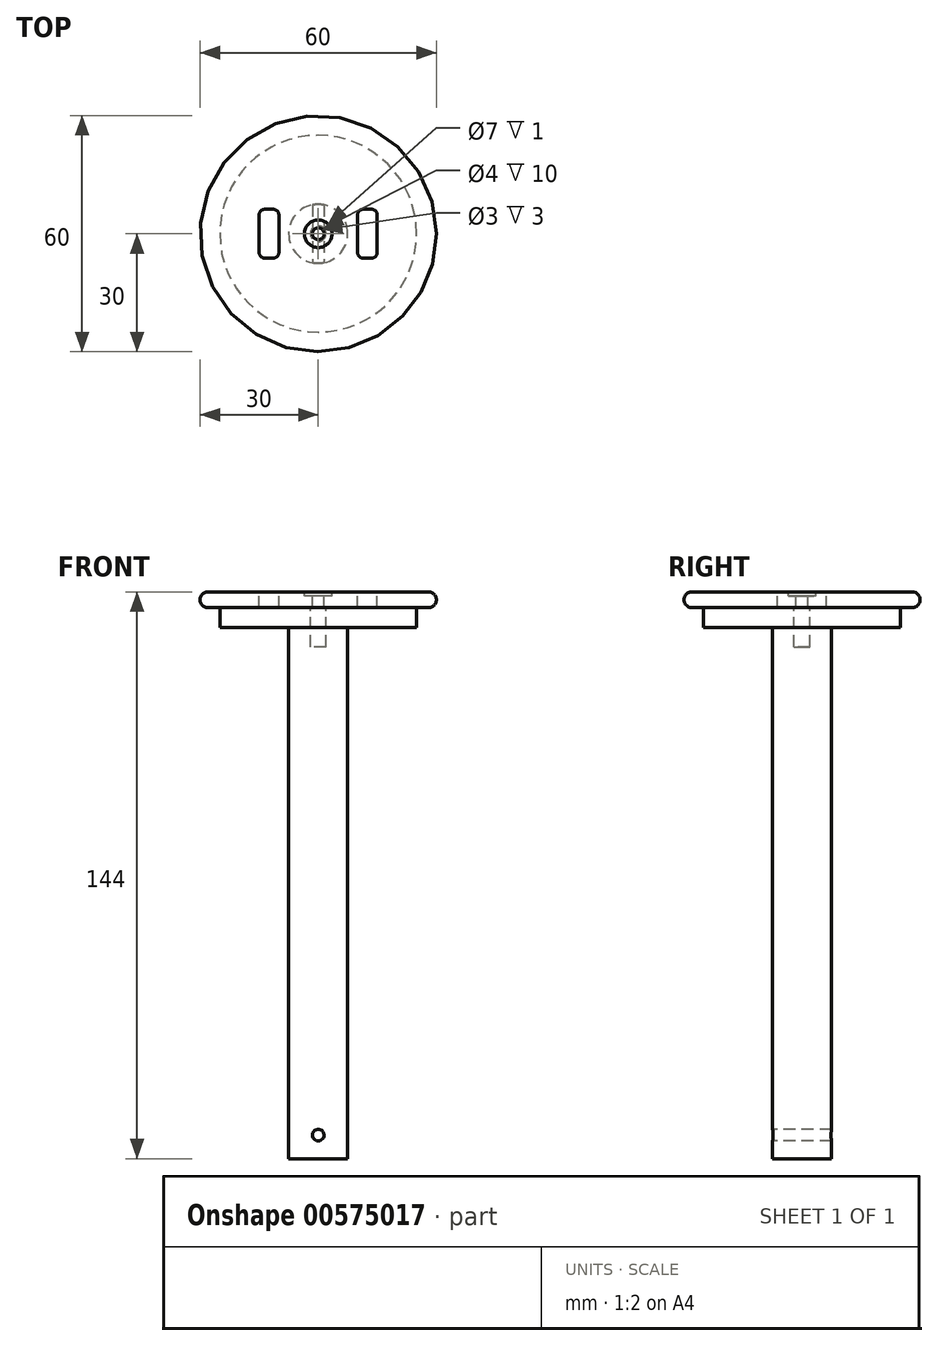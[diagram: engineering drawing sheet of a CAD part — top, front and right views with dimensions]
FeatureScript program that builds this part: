
annotation { "Feature Type Name" : "Feature", "Feature Type Description" : "" }
export const myFeature = defineFeature(function(context is Context, id is Id, definition is map)
    precondition{}
    {
        {
            var Q0;
            Q0=qCreatedBy(makeId("Top.planeOp"),FACE);
            var sketch = newSketch(context, id + "F0", { "sketchPlane" : qUnion([Q0])});
            skCircle(sketch, "E0", {"center": v(0, 0) * mm, "radius": 7.5 * mm});
            skSolve(sketch);
        }
        {
            var Q0;
            Q0 = qSketchRegion(id + "F0", true);
            extrude(context, id + "F1", {"entities" : qUnion([Q0]), "depth" : 135 * mm, "offsetDistance" : 25 * mm});
        }
        {
            var Q0;
            Q0=makeQuery(id+"F1.opExtrude","CAP_FACE",FACE,{"disambiguationData":[OSD([sQuery(id+"F0.wireOp",EDGE,"E0")])],"isStart":false});
            var sketch = newSketch(context, id + "F2", { "sketchPlane" : qUnion([Q0])});
            skCircle(sketch, "E1", {"center": v(0, 0) * mm, "radius": 25 * mm});
            skSolve(sketch);
        }
        {
            var Q0;
            Q0 = qSketchRegion(id + "F2", true);
            extrude(context, id + "F3", {"entities" : qUnion([Q0]), "operationType" : NewBodyOperationType.ADD, "depth" : 5 * mm, "offsetDistance" : 25 * mm});
        }
        {
            var Q0;
            Q0=qCreatedBy(makeId("Front.planeOp"),FACE);
            var sketch = newSketch(context, id + "F4", { "sketchPlane" : qUnion([Q0])});
            skCircle(sketch, "E2", {"center": v(0, 6) * mm, "radius": 1.5 * mm});
            skSolve(sketch);
        }
        {
            var Q0;
            Q0 = qSketchRegion(id + "F4", true);
            extrude(context, id + "F5", {"entities" : qUnion([Q0]), "operationType" : NewBodyOperationType.REMOVE, "endBound" : BoundingType.UP_TO_NEXT, "oppositeDirection" : true, "depth" : 25 * mm, "offsetDistance" : 25 * mm, "hasSecondDirection" : true, "secondDirectionBound" : SecondDirectionBoundingType.UP_TO_NEXT, "secondDirectionOppositeDirection" : false, "secondDirectionDepth" : 25 * mm});
        }
        {
            var Q0;
            Q0=makeQuery(id+"F3.opExtrude","CAP_FACE",FACE,{"disambiguationData":[OSD([sQuery(id+"F2.wireOp",EDGE,"E1")])],"isStart":false});
            var sketch = newSketch(context, id + "F6", { "sketchPlane" : qUnion([Q0])});
            skCircle(sketch, "E3", {"center": v(0, 0) * mm, "radius": 2 * mm});
            skSolve(sketch);
        }
        {
            var Q0;
            Q0 = qSketchRegion(id + "F6", true);
            extrude(context, id + "F7", {"entities" : qUnion([Q0]), "operationType" : NewBodyOperationType.REMOVE, "oppositeDirection" : true, "depth" : 10 * mm, "offsetDistance" : 25 * mm});
        }
        {
            var Q0;
            Q0=makeQuery(id+"F3.opExtrude","CAP_FACE",FACE,{"disambiguationData":[OSD([sQuery(id+"F2.wireOp",EDGE,"E1")])],"isStart":false});
            var sketch = newSketch(context, id + "F8", { "sketchPlane" : qUnion([Q0])});
            skCircle(sketch, "E4.0", {"center": v(0, 0) * mm, "radius": 2 * mm});
            skCircle(sketch, "E5", {"center": v(0, 0) * mm, "radius": 30 * mm});
            skSolve(sketch);
        }
        {
            var Q0;
            Q0 = qSketchRegion(id + "F8", true);
            extrude(context, id + "F9", {"entities" : qUnion([Q0]), "depth" : 4 * mm, "offsetDistance" : 25 * mm});
        }
        {
            var Q0;
            Q0=makeQuery(id+"F9.opExtrude","CAP_FACE",FACE,{"disambiguationData":[OSD([sQuery(id+"F8.wireOp",EDGE,"E4.0"),sQuery(id+"F8.wireOp",EDGE,"E5")])],"isStart":false});
            var sketch = newSketch(context, id + "F10", { "sketchPlane" : qUnion([Q0])});
            skLineSegment(sketch, "E6.bottom", {"start": v(11.5, 6.25) * mm, "end": v(13.5, 6.25) * mm});
            skLineSegment(sketch, "E6.top", {"start": v(11.5, -6.25) * mm, "end": v(13.5, -6.25) * mm});
            skLineSegment(sketch, "E6.left", {"start": v(10, 4.75) * mm, "end": v(10, -4.75) * mm});
            skLineSegment(sketch, "E6.right", {"start": v(15, 4.75) * mm, "end": v(15, -4.75) * mm});
            skPoint(sketch, "E6.middle", {"position": v(12.5, 0) * mm});
            skPoint(sketch, "E7.visualSharp", {"position": v(10, 6.25) * mm});
            skArc(sketch, "E7.filletArc", {"start": v(11.5, 6.25) * mm, "mid": v(10.44, 5.81) * mm, "end": v(10, 4.75) * mm});
            skPoint(sketch, "E8.visualSharp", {"position": v(15, 6.25) * mm});
            skArc(sketch, "E8.filletArc", {"start": v(15, 4.75) * mm, "mid": v(14.56, 5.81) * mm, "end": v(13.5, 6.25) * mm});
            skPoint(sketch, "E9.visualSharp", {"position": v(10, -6.25) * mm});
            skArc(sketch, "E9.filletArc", {"start": v(10, -4.75) * mm, "mid": v(10.44, -5.81) * mm, "end": v(11.5, -6.25) * mm});
            skPoint(sketch, "E10.visualSharp", {"position": v(15, -6.25) * mm});
            skArc(sketch, "E10.filletArc", {"start": v(13.5, -6.25) * mm, "mid": v(14.56, -5.81) * mm, "end": v(15, -4.75) * mm});
            skArc(sketch, "E11.MirrorCS", {"start": v(-11.5, 6.25) * mm, "mid": v(-10.44, 5.81) * mm, "end": v(-10, 4.75) * mm});
            skArc(sketch, "E12.MirrorCS", {"start": v(-15, 4.75) * mm, "mid": v(-14.56, 5.81) * mm, "end": v(-13.5, 6.25) * mm});
            skLineSegment(sketch, "E13.MirrorCS", {"start": v(-11.5, -6.25) * mm, "end": v(-13.5, -6.25) * mm});
            skLineSegment(sketch, "E14.MirrorCS", {"start": v(-11.5, 6.25) * mm, "end": v(-13.5, 6.25) * mm});
            skArc(sketch, "E15.MirrorCS", {"start": v(-13.5, -6.25) * mm, "mid": v(-14.56, -5.81) * mm, "end": v(-15, -4.75) * mm});
            skArc(sketch, "E16.MirrorCS", {"start": v(-10, -4.75) * mm, "mid": v(-10.44, -5.81) * mm, "end": v(-11.5, -6.25) * mm});
            skLineSegment(sketch, "E17.MirrorCS", {"start": v(-15, 4.75) * mm, "end": v(-15, -4.75) * mm});
            skPoint(sketch, "E18.MirrorP", {"position": v(-15, 6.25) * mm});
            skPoint(sketch, "E19.MirrorP", {"position": v(-10, 6.25) * mm});
            skLineSegment(sketch, "E20.MirrorCS", {"start": v(-10, 4.75) * mm, "end": v(-10, -4.75) * mm});
            skPoint(sketch, "E21.MirrorP", {"position": v(-12.5, 0) * mm});
            skPoint(sketch, "E22.MirrorP", {"position": v(-10, -6.25) * mm});
            skPoint(sketch, "E23.MirrorP", {"position": v(-15, -6.25) * mm});
            skSolve(sketch);
        }
        {
            var Q0;
            Q0 = qSketchRegion(id + "F10", true);
            extrude(context, id + "F11", {"entities" : qUnion([Q0]), "operationType" : NewBodyOperationType.REMOVE, "endBound" : BoundingType.UP_TO_NEXT, "oppositeDirection" : true, "depth" : 25 * mm, "offsetDistance" : 25 * mm});
        }
        {
            var Q0;
            Q0=makeQuery(id+"F9.opExtrude","CAP_FACE",FACE,{"disambiguationData":[OSD([sQuery(id+"F8.wireOp",EDGE,"E4.0"),sQuery(id+"F8.wireOp",EDGE,"E5")])],"isStart":false});
            var sketch = newSketch(context, id + "F12", { "sketchPlane" : qUnion([Q0])});
            skCircle(sketch, "E24", {"center": v(0, 0) * mm, "radius": 3.5 * mm});
            skCircle(sketch, "E25", {"center": v(0, 0) * mm, "radius": 1.5 * mm});
            skSolve(sketch);
        }
        {
            var Q0;
            Q0=makeQuery(id+"F12.imprint","IMPRINT",FACE,{"disambiguationData":[TD([[makeQuery(id+"F12.imprint","IMPRINT",EDGE,{"derivedFrom":sQuery(id+"F12.wireOp",EDGE,"E25")}),-1.0]])]});
            var Q1;
            Q1=makeQuery(id+"F9.opExtrude","CAP_FACE",FACE,{"disambiguationData":[OSD([sQuery(id+"F8.wireOp",EDGE,"E4.0"),sQuery(id+"F8.wireOp",EDGE,"E5")])],"isStart":true});
            extrude(context, id + "F13", {"entities" : qUnion([Q0]), "operationType" : NewBodyOperationType.ADD, "endBound" : BoundingType.UP_TO_SURFACE, "oppositeDirection" : true, "depth" : 25 * mm, "endBoundEntityFace" : qUnion([Q1]), "offsetDistance" : 25 * mm});
        }
        {
            var Q0;
            Q0=makeQuery(id+"F12.imprint","IMPRINT",FACE,{"disambiguationData":[TD([[makeQuery(id+"F12.imprint","IMPRINT",EDGE,{"derivedFrom":sQuery(id+"F12.wireOp",EDGE,"E24")}),1.0]])]});
            var Q1;
            Q1=makeQuery(id+"F12.imprint","IMPRINT",FACE,{"disambiguationData":[TD([[makeQuery(id+"F12.imprint","IMPRINT",EDGE,{"derivedFrom":sQuery(id+"F12.wireOp",EDGE,"E25")}),-1.0]])]});
            extrude(context, id + "F14", {"entities" : qUnion([Q0, Q1]), "operationType" : NewBodyOperationType.REMOVE, "oppositeDirection" : true, "depth" : 1 * mm, "offsetDistance" : 25 * mm});
        }
        {
            var Q0;
            Q0=makeQuery(id+"F9.opExtrude","CAP_EDGE",EDGE,{"disambiguationData":[OSD([sQuery(id+"F8.wireOp",EDGE,"E5")])],"isStart":false});
            var Q1;
            Q1=makeQuery(id+"F9.opExtrude","CAP_EDGE",EDGE,{"disambiguationData":[OSD([sQuery(id+"F8.wireOp",EDGE,"E5")])],"isStart":true});
            fillet(context, id + "F15", {"entities" : qUnion([Q0, Q1]), "tangentPropagation" : true, "radius" : 2 * mm, "defaultsChanged" : true, "vertexSettings" : [], "allowEdgeOverflow" : false});
        }
    });
